# Revit family: Shower-Valve_Trim-KOHLER-Composed-K-T73135
name_source: partatom
category: Specialty Equipment
revit_build: Autodesk Revit 2015 (Build: 20140606_1530(x64)
units: mm (PartAtom-declared; Revit-internal decimal feet)

## types (4) — shared parameters
ADA Compliant = Yes
Assembly Code = C1030200
Date Modified = 09/24/2018
Default Elevation = 42"
Height = 3 7/8"
Length = 3 5/16"
Manufacturer = KOHLER Co.
MasterFormat 1995 = 10820
MasterFormat 2004 = 10.28.13
Material = Premium Material Construction
Product Documentation Link = http://www.us.kohler.com
Product Name = Composed
Product Page URL = http://www.us.kohler.com
URL = https://www.us.kohler.com
Width = 3 7/8"

## per-type parameters (varying)
| type | Description | Finish | Model | T73135_3 | T73135_4 | Type |
| Cross Handle, CP-Polished Chrome | Volume control valve trim with cross handle | Kohler-Metal-CP-Polished_Chrome | K-T73135-3-CP | Yes | No | 1 |
| Lever Handle, CP-Polished Chrome | Volume control valve trim with lever handle | Kohler-Metal-CP-Polished_Chrome | K-T73135-4-CP | No | Yes | 3 |
| Cross Handle, TT-Vibrant Titanium | Volume control valve trim with cross handle | Kohler-Metal-TT-Vibrant_Titanium | K-T73135-3-TT | Yes | No | 2 |
| Lever Handle, TT-Vibrant Titanium | Volume control valve trim with lever handle | Kohler-Metal-TT-Vibrant_Titanium | K-T73135-4-TT | No | Yes | 4 |

## geometry (parser evidence)
native form markers: Sweep x6
no freeform markers — native parametric forms only
